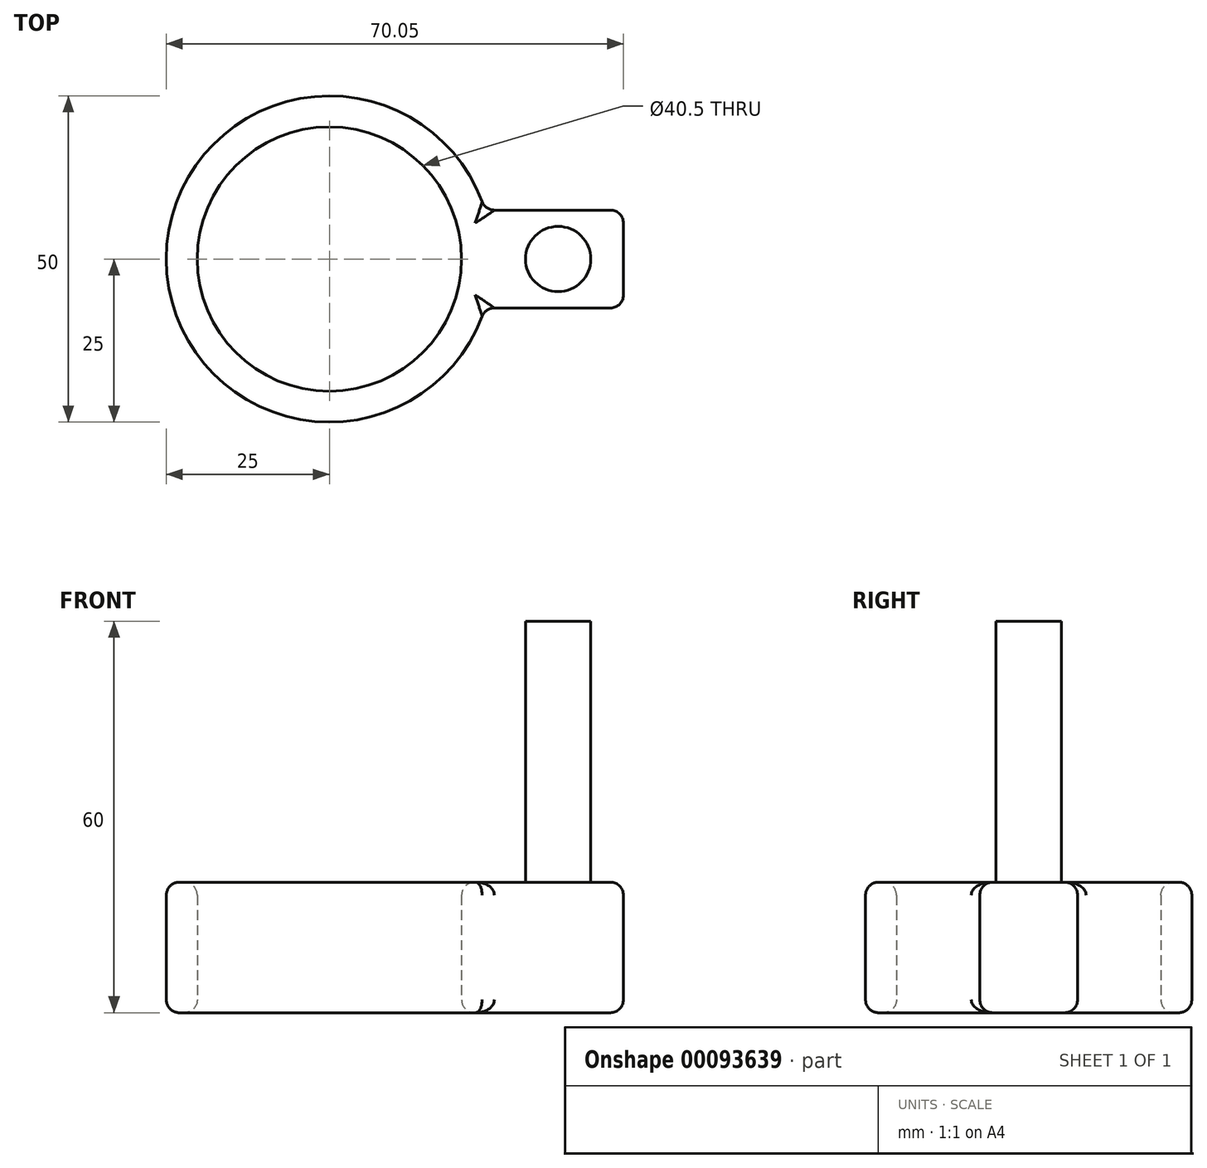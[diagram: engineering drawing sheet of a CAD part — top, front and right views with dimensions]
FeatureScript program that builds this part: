
annotation { "Feature Type Name" : "Feature", "Feature Type Description" : "" }
export const myFeature = defineFeature(function(context is Context, id is Id, definition is map)
    precondition{}
    {
        {
            var Q0;
            Q0=qCreatedBy(makeId("Top.planeOp"),FACE);
            var sketch = newSketch(context, id + "F0", { "sketchPlane" : qUnion([Q0])});
            skCircle(sketch, "E0", {"center": v(0, 0) * mm, "radius": 20.25 * mm});
            skArc(sketch, "E1", {"start": v(23.85, 7.5) * mm, "mid": v(-25, 0) * mm, "end": v(23.85, -7.5) * mm});
            skLineSegment(sketch, "E2.bottom", {"start": v(23.85, 7.5) * mm, "end": v(45.05, 7.5) * mm});
            skLineSegment(sketch, "E2.top", {"start": v(23.85, -7.5) * mm, "end": v(45.05, -7.5) * mm});
            skLineSegment(sketch, "E2.right", {"start": v(45.05, 7.5) * mm, "end": v(45.05, -7.5) * mm});
            skSolve(sketch);
        }
        {
            var Q0;
            Q0=makeQuery(id+"F0.imprint","IMPRINT",FACE,{"disambiguationData":[TD([[makeQuery(id+"F0.imprint","IMPRINT",EDGE,{"derivedFrom":sQuery(id+"F0.wireOp",EDGE,"E0")}),-1.0]])]});
            extrude(context, id + "F1", {"entities" : qUnion([Q0]), "depth" : 20 * mm});
        }
        {
            var Q0;
            Q0=makeQuery(id+"F1.opExtrude","CAP_FACE",FACE,{"disambiguationData":[OSD([sQuery(id+"F0.wireOp",EDGE,"E0"),sQuery(id+"F0.wireOp",EDGE,"E1"),sQuery(id+"F0.wireOp",EDGE,"E2.bottom"),sQuery(id+"F0.wireOp",EDGE,"E2.top"),sQuery(id+"F0.wireOp",EDGE,"E2.right")])],"isStart":false});
            var sketch = newSketch(context, id + "F2", { "sketchPlane" : qUnion([Q0])});
            skCircle(sketch, "E3", {"center": v(35.05, 0) * mm, "radius": 5 * mm});
            skSolve(sketch);
        }
        {
            var Q0;
            Q0 = qSketchRegion(id + "F2", true);
            extrude(context, id + "F3", {"entities" : qUnion([Q0]), "operationType" : NewBodyOperationType.ADD, "depth" : 40 * mm});
        }
        {
            var Q0;
            Q0=makeQuery(id+"F1.opExtrude","CAP_EDGE",EDGE,{"disambiguationData":[OSD([sQuery(id+"F0.wireOp",EDGE,"E2.top")])],"isStart":false});
            var Q1;
            Q1=makeQuery(id+"F1.opExtrude","CAP_EDGE",EDGE,{"disambiguationData":[OSD([sQuery(id+"F0.wireOp",EDGE,"E2.bottom")])],"isStart":false});
            var Q2;
            Q2=makeQuery(id+"F1.opExtrude","CAP_EDGE",EDGE,{"disambiguationData":[OSD([sQuery(id+"F0.wireOp",EDGE,"E2.right")])],"isStart":false});
            var Q3;
            Q3=makeQuery(id+"F1.opExtrude","SWEPT_EDGE",EDGE,{"disambiguationData":[OSD([sQuery(id+"F0.wireOp",EDGE,"E2.top"),sQuery(id+"F0.wireOp",EDGE,"E2.right")])]});
            var Q4;
            Q4=makeQuery(id+"F1.opExtrude","CAP_EDGE",EDGE,{"disambiguationData":[OSD([sQuery(id+"F0.wireOp",EDGE,"E2.top")])],"isStart":true});
            var Q5;
            Q5=makeQuery(id+"F1.opExtrude","CAP_EDGE",EDGE,{"disambiguationData":[OSD([sQuery(id+"F0.wireOp",EDGE,"E2.right")])],"isStart":true});
            var Q6;
            Q6=makeQuery(id+"F1.opExtrude","SWEPT_EDGE",EDGE,{"disambiguationData":[OSD([sQuery(id+"F0.wireOp",EDGE,"E2.bottom"),sQuery(id+"F0.wireOp",EDGE,"E2.right")])]});
            var Q7;
            Q7=makeQuery(id+"F1.opExtrude","CAP_EDGE",EDGE,{"disambiguationData":[OSD([sQuery(id+"F0.wireOp",EDGE,"E1")])],"isStart":false});
            var Q8;
            Q8=makeQuery(id+"F1.opExtrude","CAP_EDGE",EDGE,{"disambiguationData":[OSD([sQuery(id+"F0.wireOp",EDGE,"E0")])],"isStart":false});
            var Q9;
            Q9=makeQuery(id+"F1.opExtrude","CAP_EDGE",EDGE,{"disambiguationData":[OSD([sQuery(id+"F0.wireOp",EDGE,"E1")])],"isStart":true});
            fillet(context, id + "F4", {"entities" : qUnion([Q0, Q1, Q2, Q3, Q4, Q5, Q6, Q7, Q8, Q9]), "radius" : 2 * mm, "tangentPropagation" : true, "allowEdgeOverflow" : false});
        }
        {
            var Q0;
            Q0=makeQuery(id+"F1.opExtrude","CAP_EDGE",EDGE,{"disambiguationData":[OSD([sQuery(id+"F0.wireOp",EDGE,"E0")])],"isStart":true});
            var Q1;
            Q1=makeQuery(id+"F1.opExtrude","CAP_EDGE",EDGE,{"disambiguationData":[OSD([sQuery(id+"F0.wireOp",EDGE,"E2.bottom")])],"isStart":true});
            var Q2;
            Q2=makeQuery(id+"F1.opExtrude","SWEPT_EDGE",EDGE,{"disambiguationData":[OSD([sQuery(id+"F0.wireOp",EDGE,"E1"),sQuery(id+"F0.wireOp",EDGE,"E2.bottom")])]});
            fillet(context, id + "F5", {"entities" : qUnion([Q0, Q1, Q2]), "radius" : 2 * mm, "tangentPropagation" : true, "allowEdgeOverflow" : false});
        }
        {
            var Q0;
            Q0=makeQuery(id+"F1.opExtrude","SWEPT_EDGE",EDGE,{"disambiguationData":[OSD([sQuery(id+"F0.wireOp",EDGE,"E1"),sQuery(id+"F0.wireOp",EDGE,"E2.top")])]});
            fillet(context, id + "F6", {"entities" : qUnion([Q0]), "radius" : 2 * mm, "tangentPropagation" : true, "allowEdgeOverflow" : false});
        }
    });
